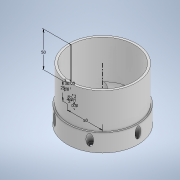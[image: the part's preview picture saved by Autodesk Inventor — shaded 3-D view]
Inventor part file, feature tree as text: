
AUTODESK INVENTOR PART (.ipt)
format: ipt  version: 2022 (Build 260153000, 153)  size: 280,064 bytes
history: native  units: mm
features: sketch x2, revolve x2, pattern_circular x2, extrude x1, fillet x1
ambient origin geometry x8: Origin, YZ Plane, XZ Plane, XY Plane, X Axis, Y Axis, Z Axis, Center Point
bodies: Solid1 (feature_tree)
feature tree (8):
  sketch  "Sketch1"  dims[d0=25.0mm d1=2.0mm]
  revolve  "Revolution1"  [1 undecoded]
  revolve  "Revolution2"  Angle=30.0deg
  pattern_circular  "Circular Pattern1"  [2 undecoded]
  extrude  "Extrusion1"  Depth=5.0mm
  fillet  "Fillet1"  Radius=4.0mm
  pattern_circular  "Circular Pattern2"  [2 undecoded]
  sketch  "Sketch2"  dims[d2=50.0mm d3=30.0deg d5=3.0mm d6=2.0mm d7=4.0mm d8=3.0mm d9=8.0mm d10=2.0mm d11=2.0mm d12=4.5mm d13=50.0mm d14=8.0mm d15=90.0deg d16=360.0deg d17=0.5mm d18=60.0mm d19=360.0deg d21=30.0deg d22=45.0deg d23=10.0mm d24=0.0mm d25=5.0mm d26=60.0mm d27=360.0deg]
note: 5 required parameter values undecoded (feature->parameter linkage not recoverable at this tier; creation-order binding heuristic only, values carry confidence <= 0.55)